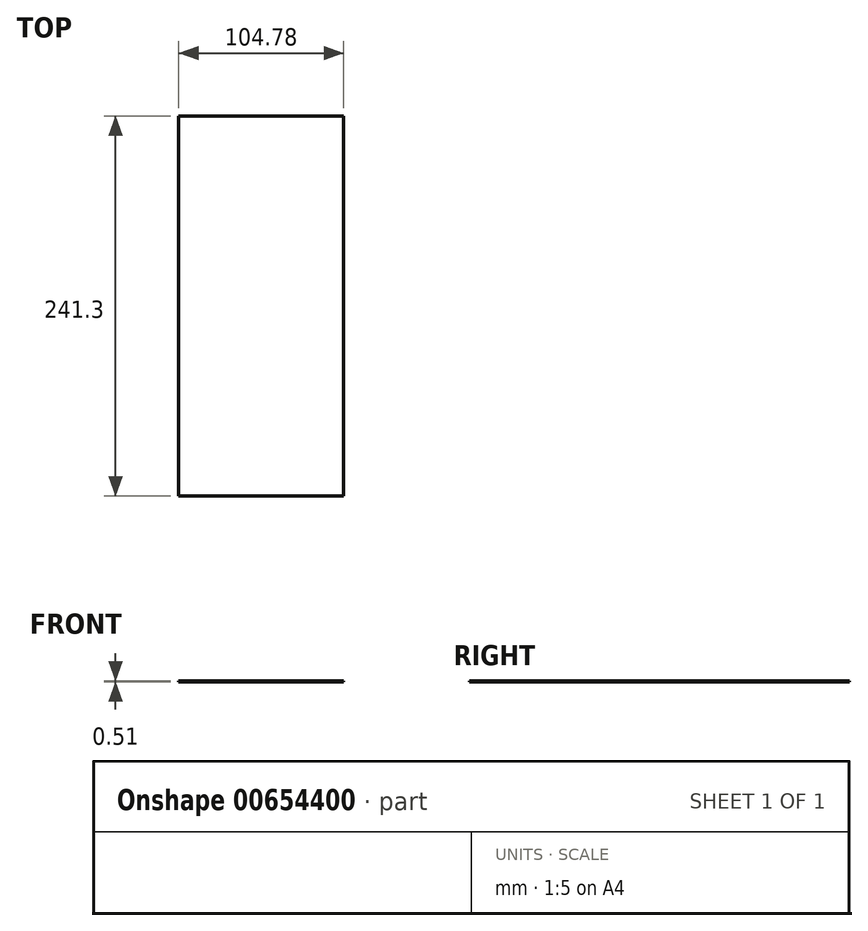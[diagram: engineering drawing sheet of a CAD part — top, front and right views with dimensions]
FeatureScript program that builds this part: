
annotation { "Feature Type Name" : "Feature", "Feature Type Description" : "" }
export const myFeature = defineFeature(function(context is Context, id is Id, definition is map)
    precondition{}
    {
        {
            var Q0;
            Q0=qCreatedBy(makeId("Top.planeOp"),FACE);
            var sketch = newSketch(context, id + "F0", { "sketchPlane" : qUnion([Q0])});
            skLineSegment(sketch, "E0.bottom", {"start": v(52.39, 120.65) * mm, "end": v(-52.39, 120.65) * mm});
            skLineSegment(sketch, "E0.top", {"start": v(52.39, -120.65) * mm, "end": v(-52.39, -120.65) * mm});
            skLineSegment(sketch, "E0.left", {"start": v(52.39, 120.65) * mm, "end": v(52.39, -120.65) * mm});
            skLineSegment(sketch, "E0.right", {"start": v(-52.39, 120.65) * mm, "end": v(-52.39, -120.65) * mm});
            skPoint(sketch, "E0.middle", {"position": v(0, 0) * mm});
            skSolve(sketch);
        }
        {
            var Q0;
            Q0=qSketchRegion(id+"F0",true);
            extrude(context, id + "F1", {"entities" : qUnion([Q0]), "depth" : 0.5 * mm, "offsetDistance" : 25.4 * mm});
        }
    });
